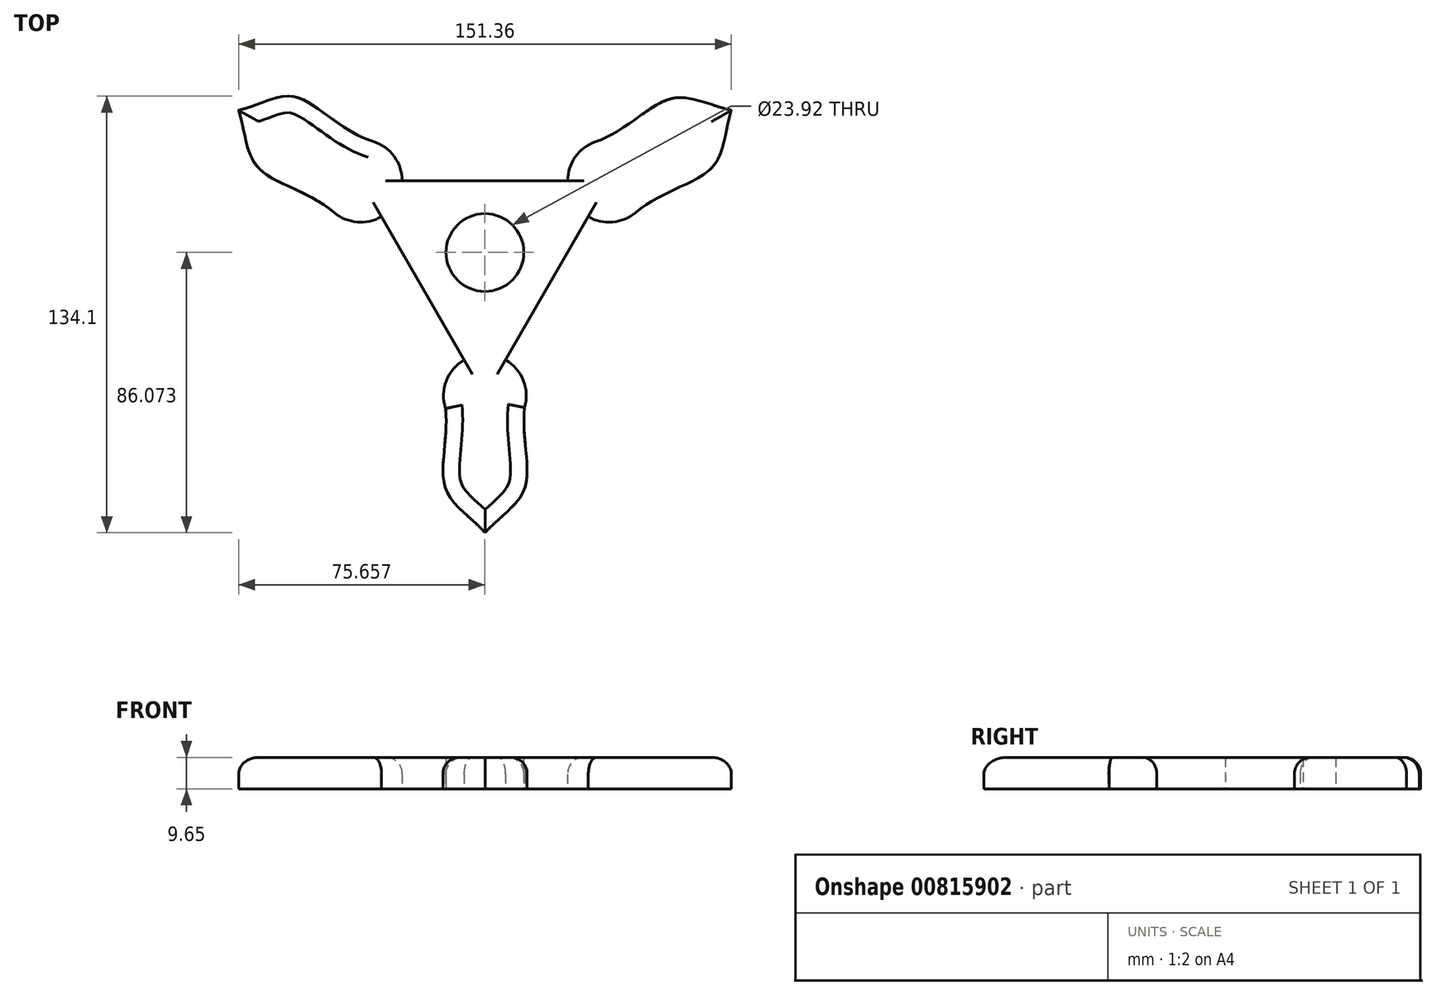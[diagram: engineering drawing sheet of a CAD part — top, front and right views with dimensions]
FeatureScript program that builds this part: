
annotation { "Feature Type Name" : "Feature", "Feature Type Description" : "" }
export const myFeature = defineFeature(function(context is Context, id is Id, definition is map)
    precondition{}
    {
        {
            var Q0;
            Q0=qCreatedBy(makeId("Top.planeOp"),FACE);
            var sketch = newSketch(context, id + "F0", { "sketchPlane" : qUnion([Q0])});
            skCircle(sketch, "E0", {"center": v(-56.96, 0) * mm, "radius": 12.7 * mm});
            skCircle(sketch, "E1", {"center": v(19.24, 0) * mm, "radius": 12.7 * mm});
            skCircle(sketch, "E2", {"center": v(-18.86, -66) * mm, "radius": 12.7 * mm});
            skLineSegment(sketch, "E3", {"start": v(-56.96, 0) * mm, "end": v(-18.86, -66) * mm});
            skLineSegment(sketch, "E4", {"start": v(19.24, 0) * mm, "end": v(-18.86, -66) * mm});
            skLineSegment(sketch, "E5", {"start": v(-56.96, 0) * mm, "end": v(19.24, 0) * mm});
            skCircle(sketch, "E6", {"center": v(-18.86, -22) * mm, "radius": 11.96 * mm});
            skLineSegment(sketch, "E7", {"start": v(-56.96, 0) * mm, "end": v(-18.86, -22) * mm});
            skLineSegment(sketch, "E8", {"start": v(-18.86, -22) * mm, "end": v(19.24, 0) * mm});
            skLineSegment(sketch, "E9", {"start": v(-18.86, -66) * mm, "end": v(-18.86, -22) * mm});
            skFitSpline(sketch, "E10", {"points": [v(14.9, 11.93) * mm, v(38.77, 25.38) * mm, v(56.84, 21.71) * mm], "startDerivative": vector(56.94, 20.74) * mm, "endDerivative": vector(43.47, -9.15) * mm});
            skFitSpline(sketch, "E11", {"points": [v(27.4, -9.73) * mm, v(50.98, 4.23) * mm, v(56.84, 21.71) * mm], "startDerivative": vector(46.43, 38.94) * mm, "endDerivative": vector(13.81, 42.23) * mm});
            skFitSpline(sketch, "E12", {"points": [v(-6.32, -66.88) * mm, v(-6.62, -94.25) * mm, v(-18.83, -108.07) * mm], "startDerivative": vector(-10.54, -59.68) * mm, "endDerivative": vector(-29.66, -33.07) * mm});
            skFitSpline(sketch, "E13", {"points": [v(-31.34, -66.88) * mm, v(-31.04, -94.25) * mm, v(-18.83, -108.07) * mm], "startDerivative": vector(10.54, -59.68) * mm, "endDerivative": vector(29.66, -33.07) * mm});
            skFitSpline(sketch, "E14", {"points": [v(-65.13, -9.73) * mm, v(-88.66, 4.23) * mm, v(-94.52, 21.71) * mm], "startDerivative": vector(-46.42, 38.95) * mm, "endDerivative": vector(-13.81, 42.23) * mm});
            skFitSpline(sketch, "E15", {"points": [v(-53.13, 12.1) * mm, v(-77.5, 25.86) * mm, v(-94.52, 21.71) * mm], "startDerivative": vector(-57.77, 18.3) * mm, "endDerivative": vector(-43.47, -9.15) * mm});
            skLineSegment(sketch, "E16", {"start": v(-56.96, 0) * mm, "end": v(-95.32, 22.14) * mm});
            skLineSegment(sketch, "E17", {"start": v(19.24, 0) * mm, "end": v(56.84, 21.71) * mm});
            skLineSegment(sketch, "E18", {"start": v(-18.86, -66) * mm, "end": v(-18.83, -108.07) * mm});
            skSolve(sketch);
        }
        {
            var Q0;
            Q0 = qSketchRegion(id + "F0", true);
            extrude(context, id + "F1", {"entities" : qUnion([Q0]), "depth" : 9.65 * mm, "offsetDistance" : 25.4 * mm});
        }
        {
            var Q0;
            Q0=makeQuery(id+"F1.opExtrude","CAP_EDGE",EDGE,{"disambiguationData":[OSD([sQuery(id+"F0.wireOp",EDGE,"E14")])],"isStart":false});
            var Q1;
            Q1=makeQuery(id+"F1.opExtrude","CAP_EDGE",EDGE,{"disambiguationData":[OSD([sQuery(id+"F0.wireOp",EDGE,"E15")])],"isStart":false});
            fillet(context, id + "F2", {"entities" : qUnion([Q0, Q1]), "radius" : 5.08 * mm, "tangentPropagation" : true, "allowEdgeOverflow" : false});
        }
        {
            var Q0;
            Q0=makeQuery(id+"F1.opExtrude","CAP_EDGE",EDGE,{"disambiguationData":[OSD([sQuery(id+"F0.wireOp",EDGE,"E13")])],"isStart":false});
            var Q1;
            Q1=makeQuery(id+"F1.opExtrude","CAP_EDGE",EDGE,{"disambiguationData":[OSD([sQuery(id+"F0.wireOp",EDGE,"E12")])],"isStart":false});
            var Q2;
            {var subQ0=sQuery(id+"F0.wireOp",EDGE,"E2");Q2=makeQuery(id+"F1.opExtrude","CAP_EDGE",EDGE,{"disambiguationData":[OSD([subQ0]),TDD([makeQuery(id+"F0.imprint","IMPRINT",EDGE,{"disambiguationData":[TD([[makeQuery(id+"F0.imprint","INTERSECT",VERTEX,{"derivedFrom":[subQ0,sQuery(id+"F0.wireOp",EDGE,"E13")]}),1.0]])],"derivedFrom":subQ0})])],"isStart":false});}
            var Q3;
            {var subQ0=sQuery(id+"F0.wireOp",EDGE,"E2");Q3=makeQuery(id+"F1.opExtrude","CAP_EDGE",EDGE,{"disambiguationData":[OSD([subQ0]),TDD([makeQuery(id+"F0.imprint","IMPRINT",EDGE,{"disambiguationData":[TD([[makeQuery(id+"F0.imprint","INTERSECT",VERTEX,{"derivedFrom":[subQ0,sQuery(id+"F0.wireOp",EDGE,"E12")]}),-1.0]])],"derivedFrom":subQ0})])],"isStart":false});}
            var Q4;
            {var subQ0=sQuery(id+"F0.wireOp",EDGE,"E1");Q4=makeQuery(id+"F1.opExtrude","CAP_EDGE",EDGE,{"disambiguationData":[OSD([subQ0]),TDD([makeQuery(id+"F0.imprint","IMPRINT",EDGE,{"disambiguationData":[TD([[makeQuery(id+"F0.imprint","INTERSECT",VERTEX,{"derivedFrom":[subQ0,sQuery(id+"F0.wireOp",EDGE,"E10")]}),-1.0]])],"derivedFrom":subQ0})])],"isStart":false});}
            var Q5;
            Q5=makeQuery(id+"F1.opExtrude","CAP_EDGE",EDGE,{"disambiguationData":[OSD([sQuery(id+"F0.wireOp",EDGE,"E11")])],"isStart":false});
            fillet(context, id + "F3", {"entities" : qUnion([Q0, Q1, Q2, Q3, Q4, Q5]), "radius" : 5.08 * mm, "tangentPropagation" : true, "allowEdgeOverflow" : false});
        }
    });
